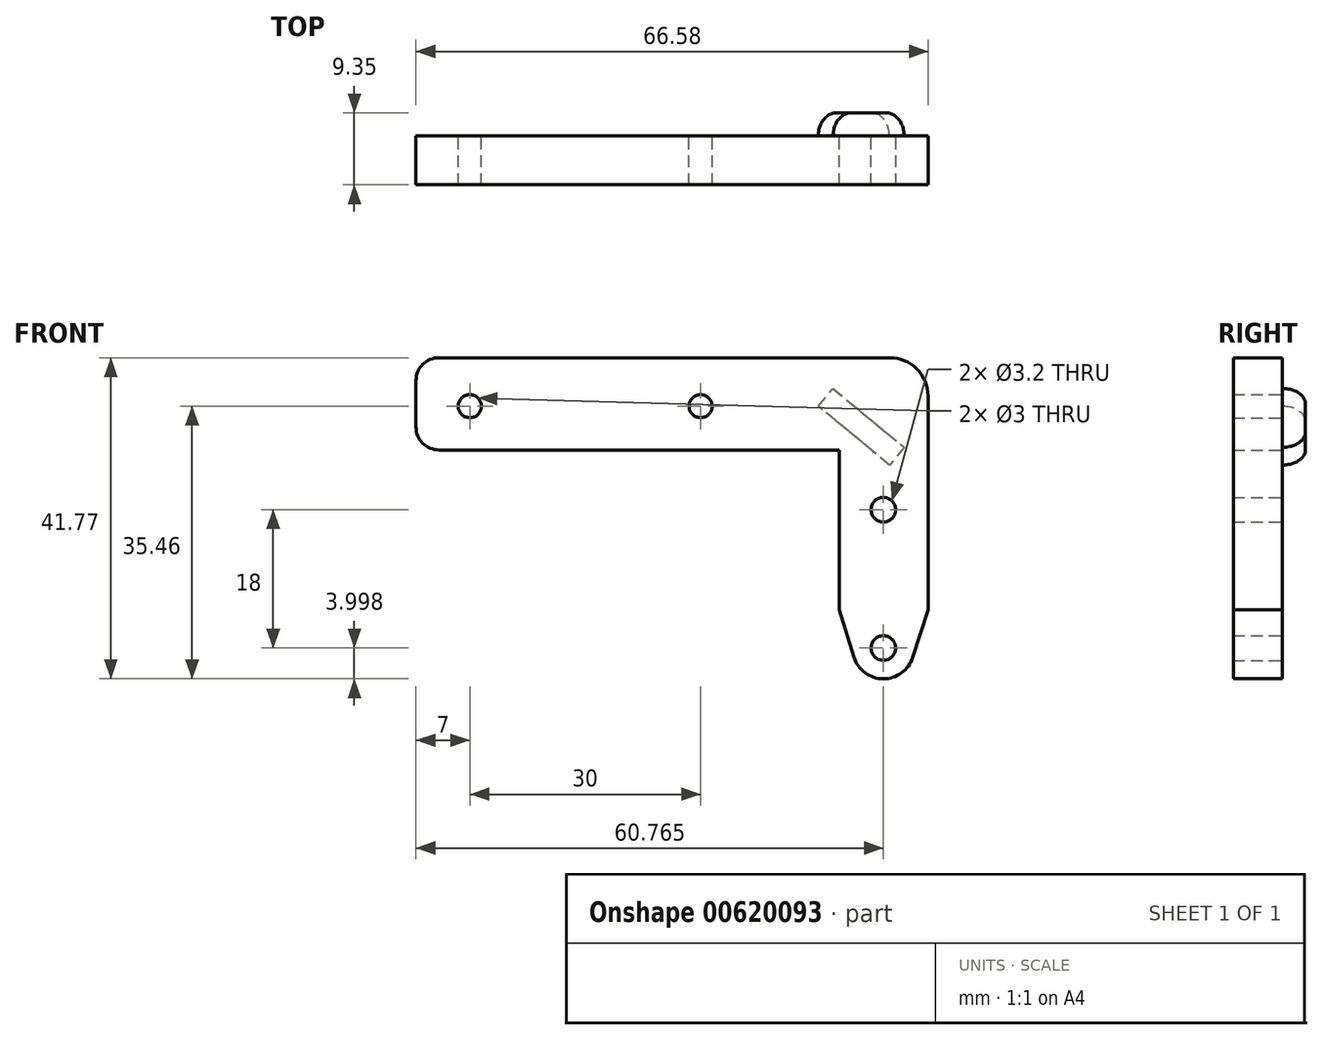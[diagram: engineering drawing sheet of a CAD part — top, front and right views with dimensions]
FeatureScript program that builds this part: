
annotation { "Feature Type Name" : "Feature", "Feature Type Description" : "" }
export const myFeature = defineFeature(function(context is Context, id is Id, definition is map)
    precondition{}
    {
        {
            var Q0;
            Q0=qCreatedBy(makeId("Front.planeOp"),FACE);
            var sketch = newSketch(context, id + "F0", { "sketchPlane" : qUnion([Q0])});
            skLineSegment(sketch, "E0.bottom", {"start": v(-19, 6.31) * mm, "end": v(33, 6.31) * mm});
            skLineSegment(sketch, "E0.top", {"start": v(-19, -5.69) * mm, "end": v(33, -5.69) * mm});
            skLineSegment(sketch, "E0.left", {"start": v(-22, 3.31) * mm, "end": v(-22, -2.69) * mm});
            skCircle(sketch, "E1", {"center": v(15, 0) * mm, "radius": 1.5 * mm, "construction": true});
            skCircle(sketch, "E2.MirrorC", {"center": v(-15, 0) * mm, "radius": 1.5 * mm, "construction": true});
            skCircle(sketch, "E3", {"center": v(38.77, -31.46) * mm, "radius": 1.6 * mm, "construction": true});
            skCircle(sketch, "E4.MirrorC", {"center": v(38.77, -13.46) * mm, "radius": 1.6 * mm, "construction": true});
            skArc(sketch, "E5.MirrorC", {"start": v(42.57, -32.69) * mm, "mid": v(38.75, -35.46) * mm, "end": v(34.95, -32.66) * mm});
            skLineSegment(sketch, "E6.bottom", {"start": v(44.58, -18.46) * mm, "end": v(44.58, -26.46) * mm});
            skLineSegment(sketch, "E6.top", {"start": v(33, -18.46) * mm, "end": v(33, -26.46) * mm});
            skPoint(sketch, "E6.middle", {"position": v(38.79, -22.46) * mm});
            skLineSegment(sketch, "E7", {"start": v(33, -26.46) * mm, "end": v(34.95, -32.66) * mm});
            skLineSegment(sketch, "E8", {"start": v(44.58, -26.46) * mm, "end": v(42.57, -32.69) * mm});
            skLineSegment(sketch, "E9", {"start": v(33, -5.69) * mm, "end": v(33, -18.46) * mm});
            skLineSegment(sketch, "E10", {"start": v(44.58, -18.46) * mm, "end": v(44.58, 1.31) * mm});
            skLineSegment(sketch, "E11", {"start": v(33, 6.31) * mm, "end": v(39.58, 6.31) * mm});
            skPoint(sketch, "E12.visualSharp", {"position": v(44.58, 6.31) * mm});
            skArc(sketch, "E12.filletArc", {"start": v(44.58, 1.31) * mm, "mid": v(43.11, 4.85) * mm, "end": v(39.58, 6.31) * mm});
            skPoint(sketch, "E13.visualSharp", {"position": v(-22, -5.69) * mm});
            skArc(sketch, "E13.filletArc", {"start": v(-22, -2.69) * mm, "mid": v(-21.12, -4.8) * mm, "end": v(-19, -5.69) * mm});
            skPoint(sketch, "E14.visualSharp", {"position": v(-22, 6.31) * mm});
            skArc(sketch, "E14.filletArc", {"start": v(-19, 6.31) * mm, "mid": v(-21.12, 5.43) * mm, "end": v(-22, 3.31) * mm});
            skSolve(sketch);
        }
        {
            var Q0;
            Q0 = qSketchRegion(id + "F0", true);
            extrude(context, id + "F1", {"entities" : qUnion([Q0]), "depth" : 6.35 * mm, "offsetDistance" : 25 * mm});
        }
        {
            var Q0;
            Q0=makeQuery(id+"F0.imprint","IMPRINT",FACE,{"disambiguationData":[TD([[makeQuery(id+"F0.imprint","IMPRINT",EDGE,{"derivedFrom":sQuery(id+"F0.wireOp",EDGE,"E0.bottom")}),-1.0]])]});
            var sketch = newSketch(context, id + "F2", { "sketchPlane" : qUnion([Q0])});
            skCircle(sketch, "E15.0", {"center": v(-15, 0) * mm, "radius": 1.5 * mm});
            skCircle(sketch, "E16.0", {"center": v(15, 0) * mm, "radius": 1.5 * mm});
            skCircle(sketch, "E17.0", {"center": v(38.77, -13.46) * mm, "radius": 1.6 * mm});
            skCircle(sketch, "E18.0", {"center": v(38.77, -31.46) * mm, "radius": 1.6 * mm});
            skSolve(sketch);
        }
        {
            var Q0;
            Q0 = qSketchRegion(id + "F2", true);
            extrude(context, id + "F3", {"entities" : qUnion([Q0]), "operationType" : NewBodyOperationType.REMOVE, "endBound" : BoundingType.THROUGH_ALL, "depth" : 25 * mm, "offsetDistance" : 25 * mm});
        }
        {
            var Q0;
            Q0=makeQuery(id+"F0.imprint","IMPRINT",FACE,{"disambiguationData":[TD([[makeQuery(id+"F0.imprint","IMPRINT",EDGE,{"derivedFrom":sQuery(id+"F0.wireOp",EDGE,"E0.bottom")}),-1.0]])]});
            var sketch = newSketch(context, id + "F4", { "sketchPlane" : qUnion([Q0])});
            skLineSegment(sketch, "E19", {"start": v(32.22, 2.3) * mm, "end": v(41.46, -5.35) * mm});
            skLineSegment(sketch, "E20", {"start": v(41.46, -5.35) * mm, "end": v(39.54, -7.66) * mm});
            skLineSegment(sketch, "E21", {"start": v(39.54, -7.66) * mm, "end": v(30.3, 0) * mm});
            skLineSegment(sketch, "E22", {"start": v(30.3, 0) * mm, "end": v(32.22, 2.3) * mm});
            skSolve(sketch);
        }
        {
            var Q0;
            Q0 = qSketchRegion(id + "F4", true);
            extrude(context, id + "F5", {"entities" : qUnion([Q0]), "operationType" : NewBodyOperationType.ADD, "oppositeDirection" : true, "depth" : 3 * mm, "offsetDistance" : 25 * mm});
        }
        {
            var Q0;
            Q0=makeQuery(id+"F5.opExtrude","CAP_EDGE",EDGE,{"disambiguationData":[OSD([sQuery(id+"F4.wireOp",EDGE,"E22")])],"isStart":false});
            var Q1;
            Q1=makeQuery(id+"F5.opExtrude","CAP_EDGE",EDGE,{"disambiguationData":[OSD([sQuery(id+"F4.wireOp",EDGE,"E20")])],"isStart":false});
            fillet(context, id + "F6", {"entities" : qUnion([Q0, Q1]), "radius" : 3 * mm, "tangentPropagation" : true, "allowEdgeOverflow" : false});
        }
    });
